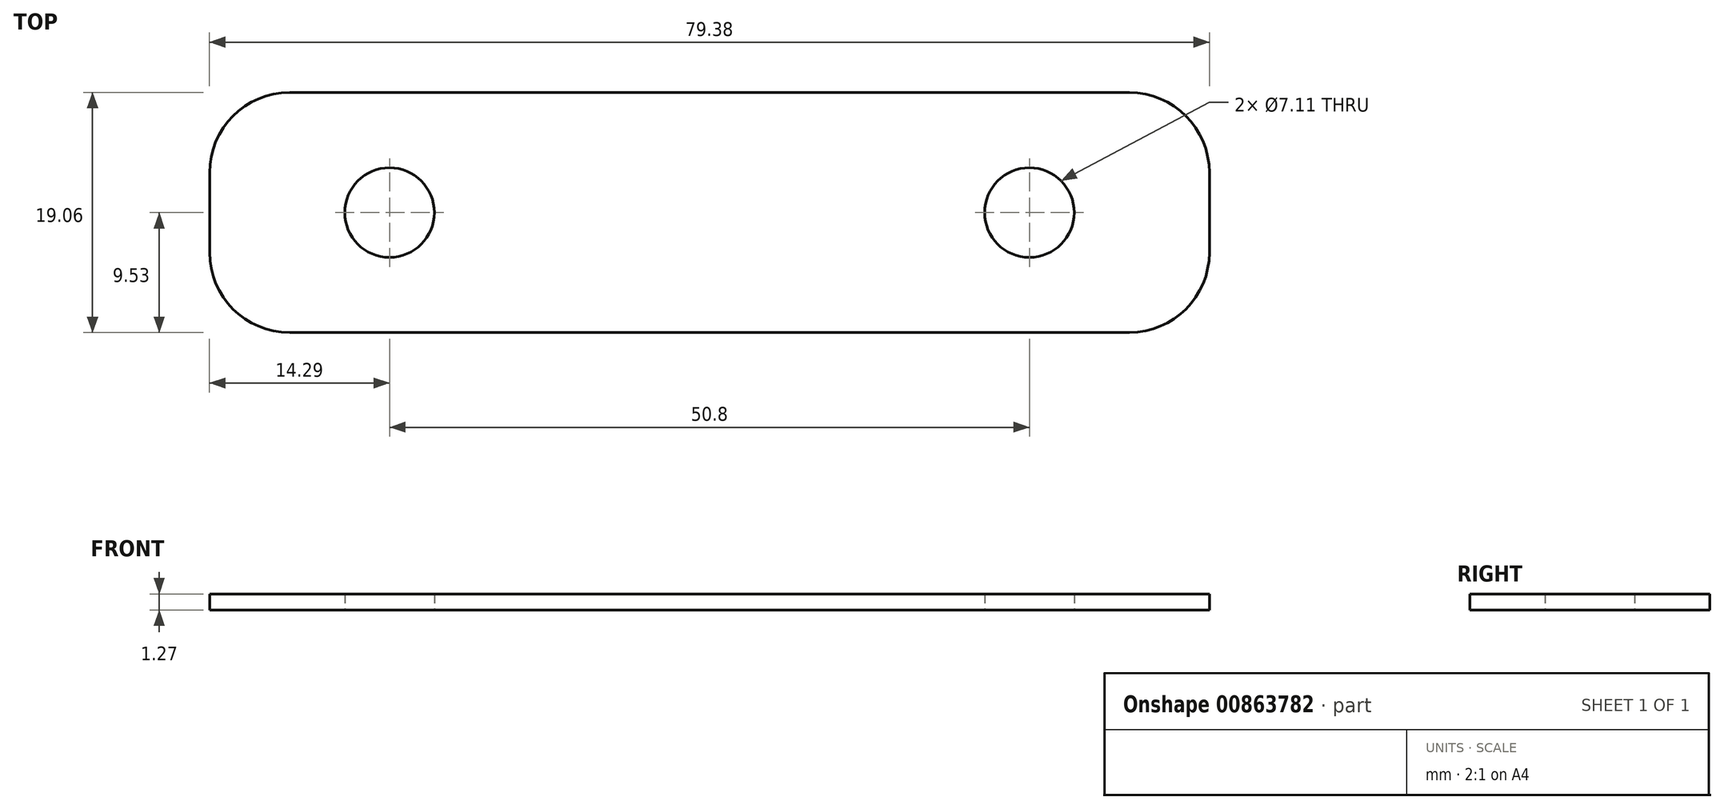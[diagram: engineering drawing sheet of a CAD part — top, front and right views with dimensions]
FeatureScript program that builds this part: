
annotation { "Feature Type Name" : "Feature", "Feature Type Description" : "" }
export const myFeature = defineFeature(function(context is Context, id is Id, definition is map)
    precondition{}
    {
        {
            var Q0;
            Q0=qCreatedBy(makeId("Top.planeOp"),FACE);
            var sketch = newSketch(context, id + "F0", { "sketchPlane" : qUnion([Q0])});
            skLineSegment(sketch, "E0.bottom", {"start": v(33.34, 9.53) * mm, "end": v(-33.34, 9.53) * mm});
            skLineSegment(sketch, "E0.top", {"start": v(33.34, -9.53) * mm, "end": v(-33.34, -9.53) * mm});
            skLineSegment(sketch, "E0.left", {"start": v(39.69, 3.18) * mm, "end": v(39.69, -3.17) * mm});
            skLineSegment(sketch, "E0.right", {"start": v(-39.69, 3.18) * mm, "end": v(-39.69, -3.18) * mm});
            skPoint(sketch, "E0.middle", {"position": v(0, 0) * mm});
            skPoint(sketch, "E1.visualSharp", {"position": v(-39.69, 9.53) * mm});
            skArc(sketch, "E1.filletArc", {"start": v(-33.34, 9.53) * mm, "mid": v(-37.83, 7.67) * mm, "end": v(-39.69, 3.17) * mm});
            skPoint(sketch, "E2.visualSharp", {"position": v(-39.69, -9.53) * mm});
            skArc(sketch, "E2.filletArc", {"start": v(-39.69, -3.18) * mm, "mid": v(-37.83, -7.67) * mm, "end": v(-33.34, -9.53) * mm});
            skPoint(sketch, "E3.visualSharp", {"position": v(39.69, 9.53) * mm});
            skArc(sketch, "E3.filletArc", {"start": v(39.69, 3.18) * mm, "mid": v(37.83, 7.67) * mm, "end": v(33.34, 9.53) * mm});
            skPoint(sketch, "E4.visualSharp", {"position": v(39.69, -9.53) * mm});
            skArc(sketch, "E4.filletArc", {"start": v(33.34, -9.53) * mm, "mid": v(37.83, -7.67) * mm, "end": v(39.69, -3.17) * mm});
            skCircle(sketch, "E5", {"center": v(-25.4, 0) * mm, "radius": 3.56 * mm});
            skCircle(sketch, "E6", {"center": v(25.4, 0) * mm, "radius": 3.56 * mm});
            skSolve(sketch);
        }
        {
            var Q0;
            Q0=makeQuery(id+"F0.imprint","IMPRINT",FACE,{"disambiguationData":[TD([[makeQuery(id+"F0.imprint","IMPRINT",EDGE,{"derivedFrom":sQuery(id+"F0.wireOp",EDGE,"E0.bottom")}),1.0]])]});
            extrude(context, id + "F1", {"entities" : qUnion([Q0]), "depth" : 1.27 * mm, "offsetDistance" : 25.4 * mm});
        }
    });
